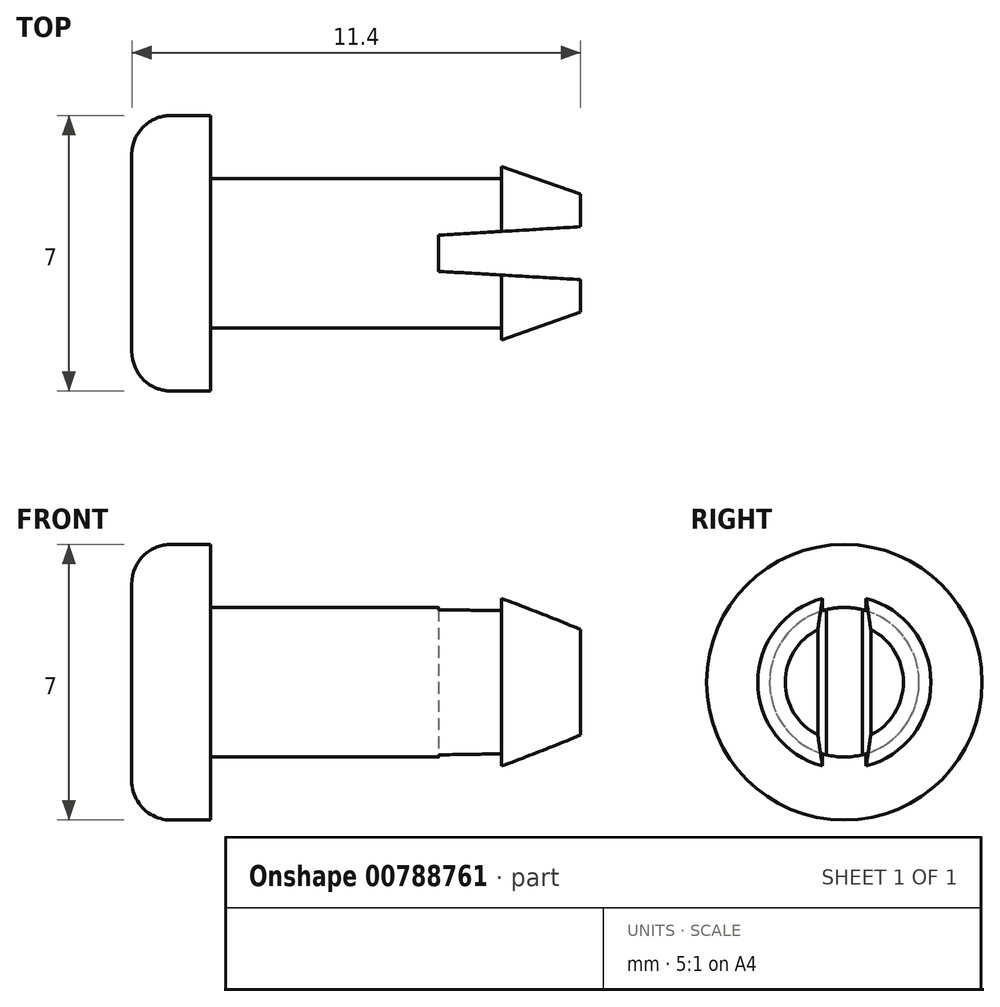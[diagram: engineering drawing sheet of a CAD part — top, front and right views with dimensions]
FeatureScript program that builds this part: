
annotation { "Feature Type Name" : "Feature", "Feature Type Description" : "" }
export const myFeature = defineFeature(function(context is Context, id is Id, definition is map)
    precondition{}
    {
        {
            var Q0;
            Q0=qCreatedBy(makeId("Top.planeOp"),FACE);
            var sketch = newSketch(context, id + "F0", { "sketchPlane" : qUnion([Q0])});
            skLineSegment(sketch, "E0.bottom", {"start": v(-50.54, 34.05) * mm, "end": v(-48.54, 34.05) * mm});
            skLineSegment(sketch, "E0.top", {"start": v(-50.54, 27.05) * mm, "end": v(-48.54, 27.05) * mm});
            skLineSegment(sketch, "E0.left", {"start": v(-50.54, 34.05) * mm, "end": v(-50.54, 27.05) * mm});
            skLineSegment(sketch, "E0.right", {"start": v(-48.54, 34.05) * mm, "end": v(-48.54, 32.45) * mm});
            skPoint(sketch, "E1", {"position": v(-48.54, 30.55) * mm});
            skLineSegment(sketch, "E2.bottom", {"start": v(-48.54, 32.45) * mm, "end": v(-41.14, 32.45) * mm});
            skLineSegment(sketch, "E2.top", {"start": v(-48.54, 28.65) * mm, "end": v(-48.54, 28.65) * mm});
            skLineSegment(sketch, "E2.left", {"start": v(-48.54, 32.45) * mm, "end": v(-48.54, 32.45) * mm});
            skLineSegment(sketch, "E2.right", {"start": v(-41.14, 32.45) * mm, "end": v(-41.14, 28.65) * mm, "construction": true});
            skPoint(sketch, "E3", {"position": v(-41.14, 30.55) * mm});
            skLineSegment(sketch, "E4", {"start": v(-50.54, 30.55) * mm, "end": v(-32.37, 30.55) * mm});
            skLineSegment(sketch, "E5", {"start": v(-41.14, 32.75) * mm, "end": v(-41.14, 32.45) * mm});
            skLineSegment(sketch, "E6", {"start": v(-41.14, 28.35) * mm, "end": v(-39.14, 29.05) * mm});
            skLineSegment(sketch, "E7", {"start": v(-39.14, 29.05) * mm, "end": v(-39.14, 32.05) * mm});
            skLineSegment(sketch, "E8", {"start": v(-39.14, 32.05) * mm, "end": v(-41.14, 32.75) * mm});
            skLineSegment(sketch, "E9", {"start": v(-41.08, 28.65) * mm, "end": v(-41.14, 28.35) * mm});
            skLineSegment(sketch, "E10", {"start": v(-48.54, 28.65) * mm, "end": v(-41.14, 28.65) * mm});
            skLineSegment(sketch, "E11", {"start": v(-48.54, 32.45) * mm, "end": v(-48.54, 28.65) * mm, "construction": true});
            skLineSegment(sketch, "E12", {"start": v(-48.38, 28.65) * mm, "end": v(-48.54, 27.05) * mm});
            skLineSegment(sketch, "E13", {"start": v(-39.14, 31.22) * mm, "end": v(-42.75, 31) * mm});
            skLineSegment(sketch, "E14", {"start": v(-42.75, 31) * mm, "end": v(-42.75, 30.1) * mm});
            skLineSegment(sketch, "E15", {"start": v(-42.75, 30.1) * mm, "end": v(-39.14, 29.88) * mm});
            skSolve(sketch);
        }
        {
            var Q0;
            {var subQ1=sQuery(id+"F0.wireOp",EDGE,"E0.bottom");Q0=makeQuery(id+"F0.imprint","IMPRINT",FACE,{"disambiguationData":[TD([[makeQuery(id+"F0.imprint","IMPRINT",EDGE,{"derivedFrom":subQ1}),-1.0]])]});}
            var Q1;
            {var subQ5=sQuery(id+"F0.wireOp",EDGE,"E13");Q1=makeQuery(id+"F0.imprint","IMPRINT",FACE,{"disambiguationData":[TD([[makeQuery(id+"F0.imprint","IMPRINT",EDGE,{"derivedFrom":subQ5}),1.0]])]});}
            var Q2;
            Q2=sQuery(id+"F0.wireOp",EDGE,"E4");
            revolve(context, id + "F1", {"surfaceOperationType" : NewSurfaceOperationType.NEW, "entities" : qUnion([Q0, Q1]), "axis" : qUnion([Q2]), "revolveType" : RevolveType.FULL});
        }
        {
            var Q0;
            {var subQ5=sQuery(id+"F0.wireOp",EDGE,"E13");Q0=makeQuery(id+"F0.imprint","IMPRINT",FACE,{"disambiguationData":[TD([[makeQuery(id+"F0.imprint","IMPRINT",EDGE,{"derivedFrom":subQ5}),1.0]])]});}
            var Q1;
            {var subQ5=sQuery(id+"F0.wireOp",EDGE,"E15");Q1=makeQuery(id+"F0.imprint","IMPRINT",FACE,{"disambiguationData":[TD([[makeQuery(id+"F0.imprint","IMPRINT",EDGE,{"derivedFrom":subQ5}),1.0]])]});}
            extrude(context, id + "F2", {"entities" : qUnion([Q0, Q1]), "operationType" : NewBodyOperationType.REMOVE, "endBound" : BoundingType.SYMMETRIC, "depth" : 25 * mm, "offsetDistance" : 25 * mm});
        }
        {
            var Q0;
            Q0=makeQuery(id+"F1.opRevolve","SWEPT_FACE",FACE,{"disambiguationData":[OSD([sQuery(id+"F0.wireOp",EDGE,"E0.left")])]});
            fillet(context, id + "F3", {"entities" : qUnion([Q0]), "radius" : 1 * mm, "tangentPropagation" : true, "allowEdgeOverflow" : false});
        }
    });
